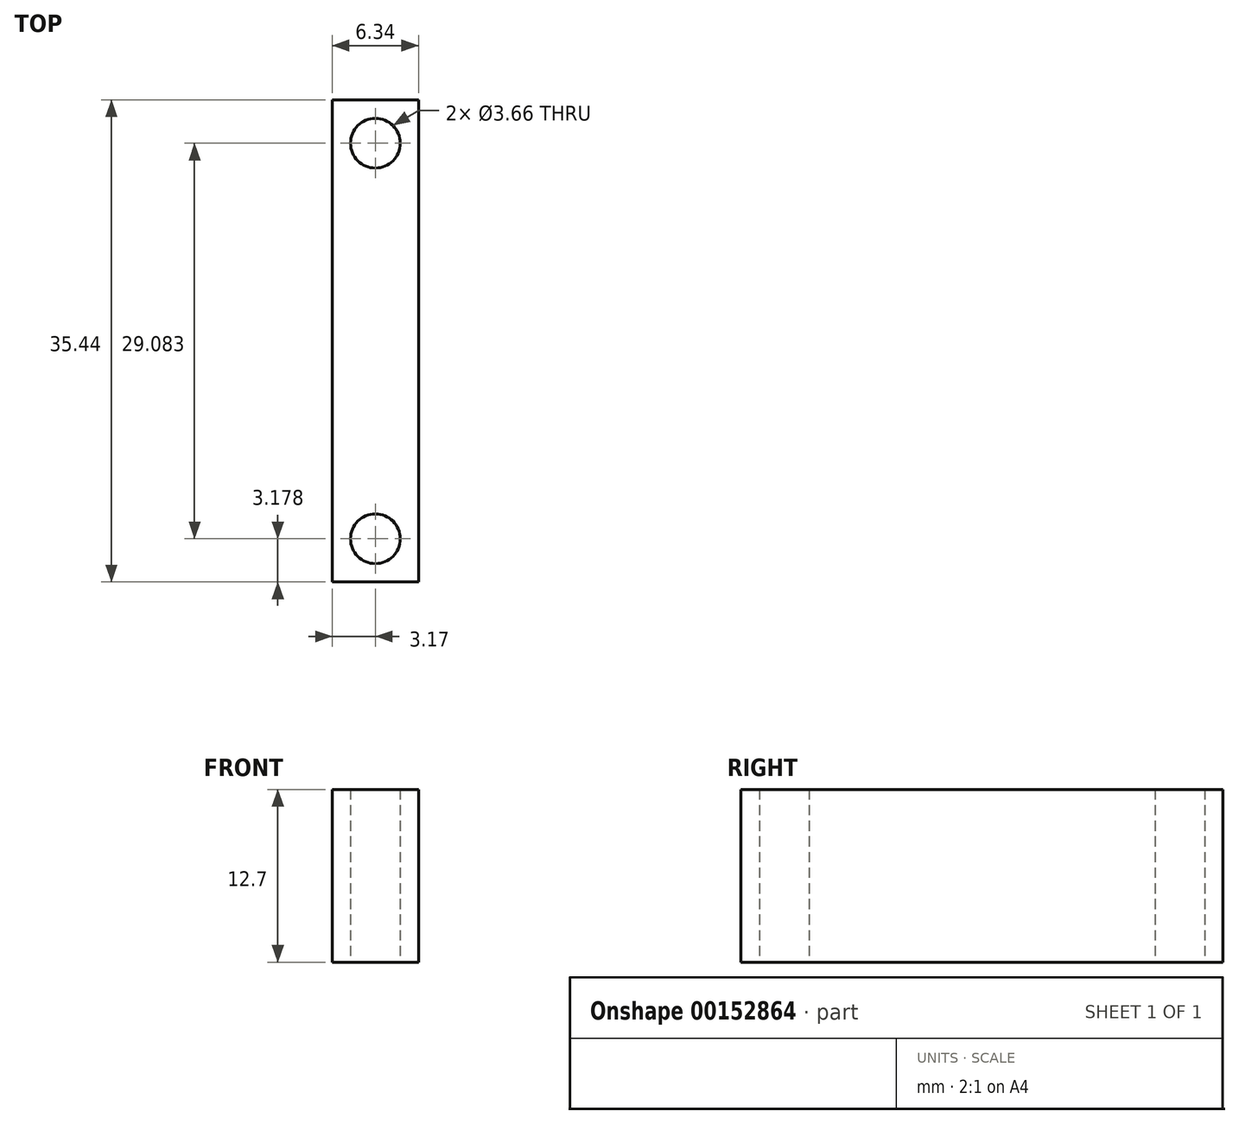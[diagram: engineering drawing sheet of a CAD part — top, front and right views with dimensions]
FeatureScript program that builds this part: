
annotation { "Feature Type Name" : "Feature", "Feature Type Description" : "" }
export const myFeature = defineFeature(function(context is Context, id is Id, definition is map)
    precondition{}
    {
        {
            var Q0;
            Q0=qCreatedBy(makeId("Top.planeOp"),FACE);
            var sketch = newSketch(context, id + "F0", { "sketchPlane" : qUnion([Q0])});
            skLineSegment(sketch, "E0.bottom", {"start": v(3.18, -17.72) * mm, "end": v(-3.18, -17.72) * mm});
            skLineSegment(sketch, "E0.top", {"start": v(3.18, 17.72) * mm, "end": v(-3.18, 17.72) * mm});
            skLineSegment(sketch, "E0.left", {"start": v(3.18, -17.72) * mm, "end": v(3.18, 17.72) * mm});
            skLineSegment(sketch, "E0.right", {"start": v(-3.18, -17.72) * mm, "end": v(-3.18, 17.72) * mm});
            skPoint(sketch, "E0.middle", {"position": v(0, 0) * mm});
            skLineSegment(sketch, "E1", {"start": v(0, 14.54) * mm, "end": v(0, 17.72) * mm, "construction": true});
            skCircle(sketch, "E2", {"center": v(0, 14.54) * mm, "radius": 1.83 * mm});
            skLineSegment(sketch, "E3", {"start": v(0, 14.54) * mm, "end": v(-3.17, 14.54) * mm, "construction": true});
            skLineSegment(sketch, "E4", {"start": v(0, -17.72) * mm, "end": v(0, -14.54) * mm, "construction": true});
            skLineSegment(sketch, "E5", {"start": v(0, -14.54) * mm, "end": v(3.18, -14.54) * mm, "construction": true});
            skCircle(sketch, "E6", {"center": v(0, -14.54) * mm, "radius": 1.83 * mm});
            skSolve(sketch);
        }
        {
            var Q0;
            Q0=makeQuery(id+"F0.imprint","IMPRINT",FACE,{"disambiguationData":[TD([[makeQuery(id+"F0.imprint","IMPRINT",EDGE,{"derivedFrom":sQuery(id+"F0.wireOp",EDGE,"E0.bottom")}),-1.0]])]});
            extrude(context, id + "F1", {"entities" : qUnion([Q0]), "depth" : 12.7 * mm});
        }
    });
